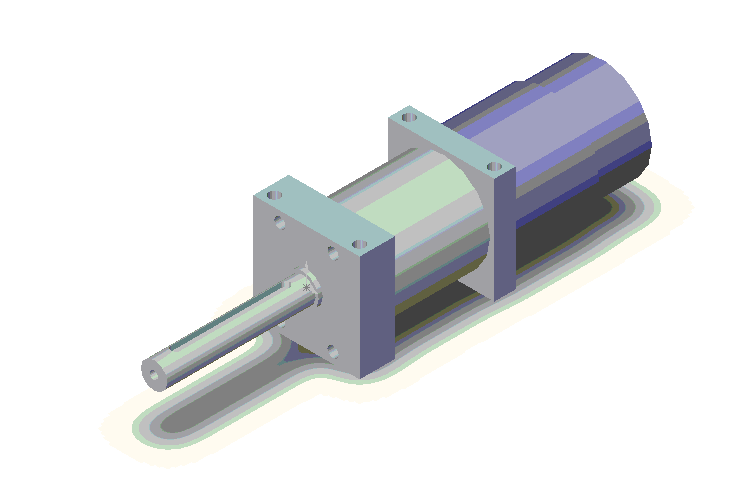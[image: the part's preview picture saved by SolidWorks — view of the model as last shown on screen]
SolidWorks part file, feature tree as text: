
SOLIDWORKS PART (.sldprt)
format: sldprt  version: not decoded by parser v0  size: 272,384 bytes
history: native  units: mm
features: sketch x14, extrude x7, cut_extrude x7, plane x2 (+8 scaffold rows collapsed)
feature tree (38):
  scaffold x8  (default folders/planes/origin — collapsed)
  sketch  "Sketch1"  dims[D13=4.0mm D14=4.0mm D15=4.0mm D16=4.0mm D1=19.05mm D2=38.1mm D3=19.05mm D4=38.1mm D5=9.525mm D6=9.53mm D7=9.53mm D8=9.53mm D9=3.81mm D10=3.81mm D11=34.29mm D12=34.29mm]
  extrude  "Base-Extrude"  Depth=12.7mm
  sketch  "Sketch2"  dims[D1=9.525mm]
  extrude  "Boss-Extrude1"  Depth=54.61mm
  plane  "Plane1"
  sketch  "Sketch3"  dims[D1=3.175mm D2=3.175mm D3=7.62mm D4=39.37mm]
  plane  "Plane2"  Offset=2.7625mm
  cut_extrude  "Cut-Extrude3"  [1 undecoded]
  sketch  "Sketch4"  dims[D1=3.0mm]
  cut_extrude  "Cut-Extrude4"  Depth=9.525mm
  sketch  "Sketch5"
  extrude  "Boss-Extrude2"  Depth=1.5mm
  sketch  "Sketch6"  dims[D1=4.0mm D2=4.0mm D3=3.81mm D4=34.29mm D5=3.81mm D6=3.81mm]
  cut_extrude  "Cut-Extrude5"  Depth=9.5mm
  sketch  "Sketch7"  dims[D1=15.24mm]
  cut_extrude  "Cut-Extrude6"  Depth=9.5mm
  sketch  "Sketch8"  dims[D1=35.0mm]
  extrude  "Boss-Extrude3"  Depth=35.56mm
  sketch  "Sketch9"
  extrude  "Boss-Extrude4"  Depth=7.62mm
  sketch  "Sketch11"  dims[D7=4.0mm D8=4.0mm D9=4.0mm D10=4.0mm D11=4.0mm D12=4.0mm D13=4.0mm D14=4.0mm D1=9.525mm D2=9.525mm D3=28.575mm D4=28.575mm D5=3.81mm D6=34.29mm D15=3.81mm D16=9.53mm D17=28.58mm D18=34.29mm]
  cut_extrude  "Cut-Extrude7"  Depth=9.525mm
  sketch  "Sketch12"  dims[c1.D3=4.0mm c1.D4=4.0mm c1.D1=3.81mm c1.D2=3.81mm c2.D3=3.81mm c2.D5=3.81mm]
  cut_extrude  "Cut-Extrude8"  Depth=9.525mm
  sketch  "Sketch13"
  cut_extrude  "Cut-Extrude9"  Depth=9.525mm
  sketch  "Sketch14"  dims[D1=35.814mm]
  extrude  "Boss-Extrude5"  Depth=50mm
  sketch  "Sketch15"  dims[D1=38.1mm]
  extrude  "Boss-Extrude6"  Depth=30mm
decode coverage: 24 of 28 modeling features carry decoded parameters
note: 1 parameter value undecoded
note: suppression state not decoded; provenance and decode notes live in map.json
